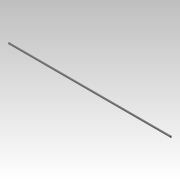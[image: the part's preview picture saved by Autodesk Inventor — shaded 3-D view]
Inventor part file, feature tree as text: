
AUTODESK INVENTOR PART (.ipt)
format: ipt  version: 2020 (Build 240168000, 168)  size: 85,504 bytes
history: native  units: mm
features: revolve x1, chamfer x1, sketch x1
ambient origin geometry x8: Origin, YZ Plane, XZ Plane, XY Plane, X Axis, Y Axis, Z Axis, Center Point
bodies: Solid1 (feature_tree)
feature tree (3):
  revolve  "Revolution1"  [1 undecoded]
  chamfer  "Chamfer1"  Distance=200.0mm
  sketch  "Sketch1"  dims[d0=0.5mm d1=1.0mm d2=200.0mm d3=90.0deg d4=0.25mm d5=2.0mm d6=45.0deg]
note: 1 required parameter value undecoded (feature->parameter linkage not recoverable at this tier; creation-order binding heuristic only, values carry confidence <= 0.55)
